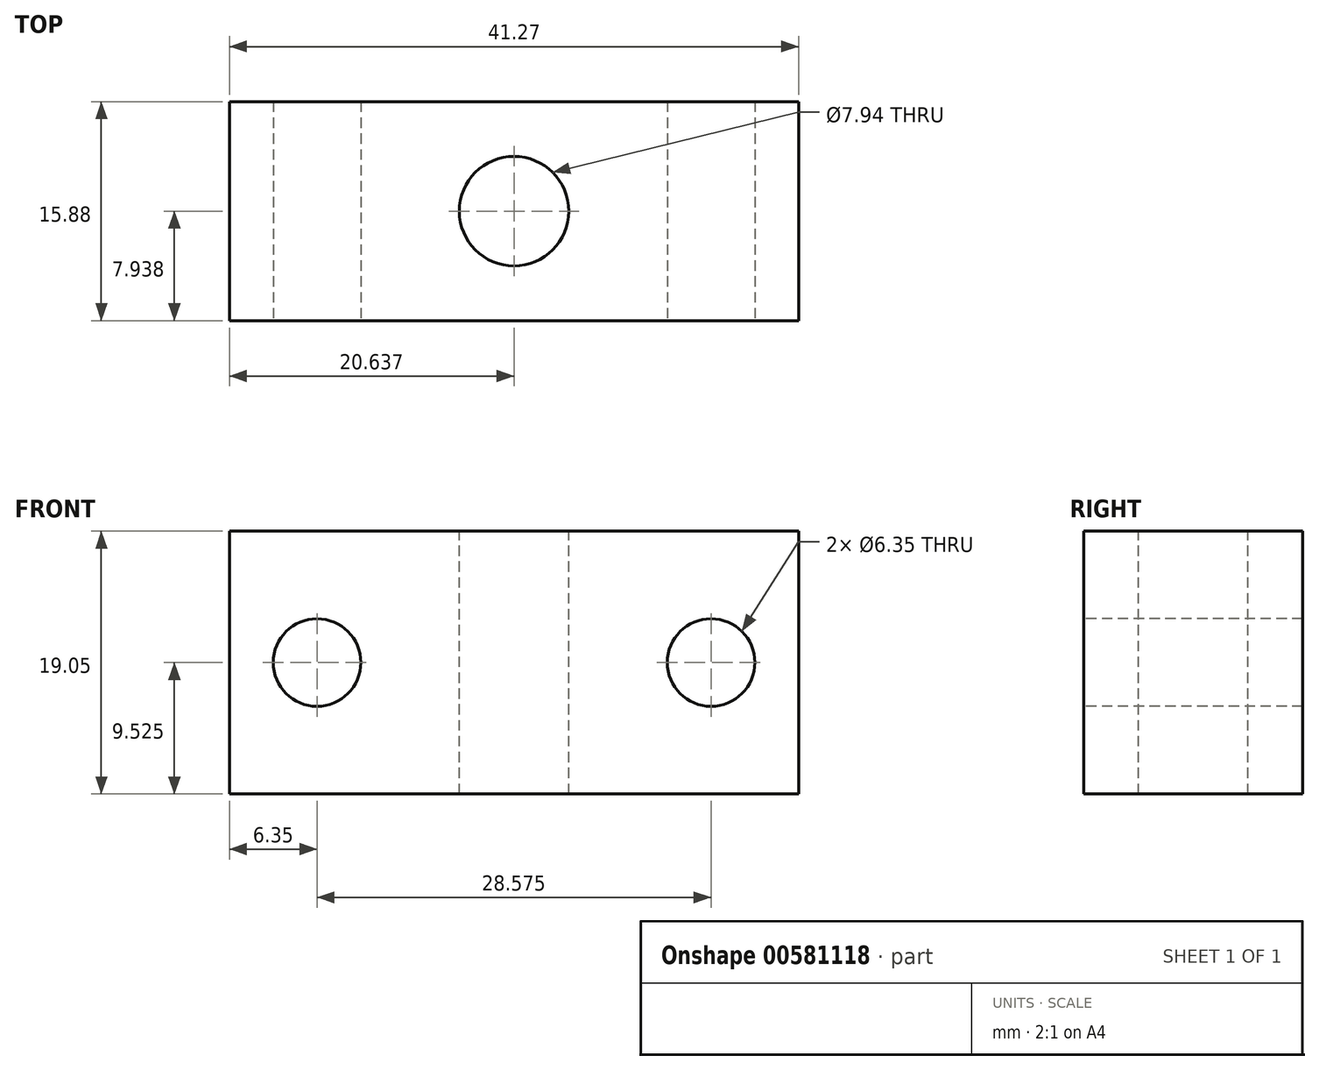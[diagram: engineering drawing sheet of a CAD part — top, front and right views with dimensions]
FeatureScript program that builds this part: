
annotation { "Feature Type Name" : "Feature", "Feature Type Description" : "" }
export const myFeature = defineFeature(function(context is Context, id is Id, definition is map)
    precondition{}
    {
        {
            var Q0;
            Q0=qCreatedBy(makeId("Top.planeOp"),FACE);
            var sketch = newSketch(context, id + "F0", { "sketchPlane" : qUnion([Q0])});
            skLineSegment(sketch, "E0.bottom", {"start": v(0, 0) * mm, "end": v(41.28, 0) * mm});
            skLineSegment(sketch, "E0.top", {"start": v(0, 15.87) * mm, "end": v(41.27, 15.87) * mm});
            skLineSegment(sketch, "E0.left", {"start": v(0, 0) * mm, "end": v(0, 15.87) * mm});
            skLineSegment(sketch, "E0.right", {"start": v(41.28, 0) * mm, "end": v(41.28, 15.87) * mm});
            skSolve(sketch);
        }
        {
            var Q0;
            Q0=makeQuery(id+"F0.imprint","IMPRINT",FACE,{"disambiguationData":[TD([[makeQuery(id+"F0.imprint","IMPRINT",EDGE,{"derivedFrom":sQuery(id+"F0.wireOp",EDGE,"E0.bottom")}),1.0]])]});
            extrude(context, id + "F1", {"entities" : qUnion([Q0]), "depth" : 19.05 * mm, "offsetDistance" : 25.4 * mm});
        }
        {
            var Q0;
            Q0=makeQuery(id+"F1.opExtrude","CAP_FACE",FACE,{"disambiguationData":[OSD([sQuery(id+"F0.wireOp",EDGE,"E0.bottom"),sQuery(id+"F0.wireOp",EDGE,"E0.top"),sQuery(id+"F0.wireOp",EDGE,"E0.left"),sQuery(id+"F0.wireOp",EDGE,"E0.right")])],"isStart":false});
            var sketch = newSketch(context, id + "F2", { "sketchPlane" : qUnion([Q0])});
            skPoint(sketch, "E1", {"position": v(20.64, 7.94) * mm});
            skPoint(sketch, "E1.positionSnap0", {"position": v(0, 7.94) * mm});
            skPoint(sketch, "E1.positionSnap1", {"position": v(20.64, 15.87) * mm});
            skSolve(sketch);
        }
        {
            var Q0;
            Q0=sQuery(id+"F2.wireOp",VERTEX,"E1");
            var Q1;
            Q1=makeQuery(id+"F1.opExtrude","SWEPT_BODY",BODY,{"disambiguationData":[OSD([sQuery(id+"F0.wireOp",EDGE,"E0.bottom"),sQuery(id+"F0.wireOp",EDGE,"E0.top"),sQuery(id+"F0.wireOp",EDGE,"E0.left"),sQuery(id+"F0.wireOp",EDGE,"E0.right")])]});
            hole(context, id + "F3", {"style" : HoleStyle.SIMPLE, "endStyle" : HoleEndStyle.THROUGH, "holeDiameter" : 7.94 * mm, "majorDiameter" : 6.35 * mm, "isTappedThrough" : true, "tappedDepth" : 12.7 * mm, "tapClearance" : 3, "locations" : qUnion([Q0]), "scope" : qUnion([Q1])});
        }
        {
            var Q0;
            Q0=makeQuery(id+"F1.opExtrude","SWEPT_FACE",FACE,{"disambiguationData":[OSD([sQuery(id+"F0.wireOp",EDGE,"E0.bottom")])]});
            var sketch = newSketch(context, id + "F4", { "sketchPlane" : qUnion([Q0])});
            skPoint(sketch, "E2", {"position": v(6.35, 9.53) * mm});
            skPoint(sketch, "E2.positionSnap0", {"position": v(0, 9.53) * mm});
            skPoint(sketch, "E3", {"position": v(34.93, 9.53) * mm});
            skPoint(sketch, "E3.positionSnap0", {"position": v(41.28, 9.53) * mm});
            skSolve(sketch);
        }
        {
            var Q0;
            Q0=sQuery(id+"F4.wireOp",VERTEX,"E2");
            var Q1;
            Q1=sQuery(id+"F4.wireOp",VERTEX,"E3");
            var Q2;
            Q2=makeQuery(id+"F1.opExtrude","SWEPT_BODY",BODY,{"disambiguationData":[OSD([sQuery(id+"F0.wireOp",EDGE,"E0.bottom"),sQuery(id+"F0.wireOp",EDGE,"E0.top"),sQuery(id+"F0.wireOp",EDGE,"E0.left"),sQuery(id+"F0.wireOp",EDGE,"E0.right")])]});
            hole(context, id + "F5", {"style" : HoleStyle.SIMPLE, "endStyle" : HoleEndStyle.THROUGH, "holeDiameter" : 6.35 * mm, "majorDiameter" : 6.35 * mm, "isTappedThrough" : true, "tappedDepth" : 12.7 * mm, "tapClearance" : 3, "locations" : qUnion([Q0, Q1]), "scope" : qUnion([Q2])});
        }
    });
